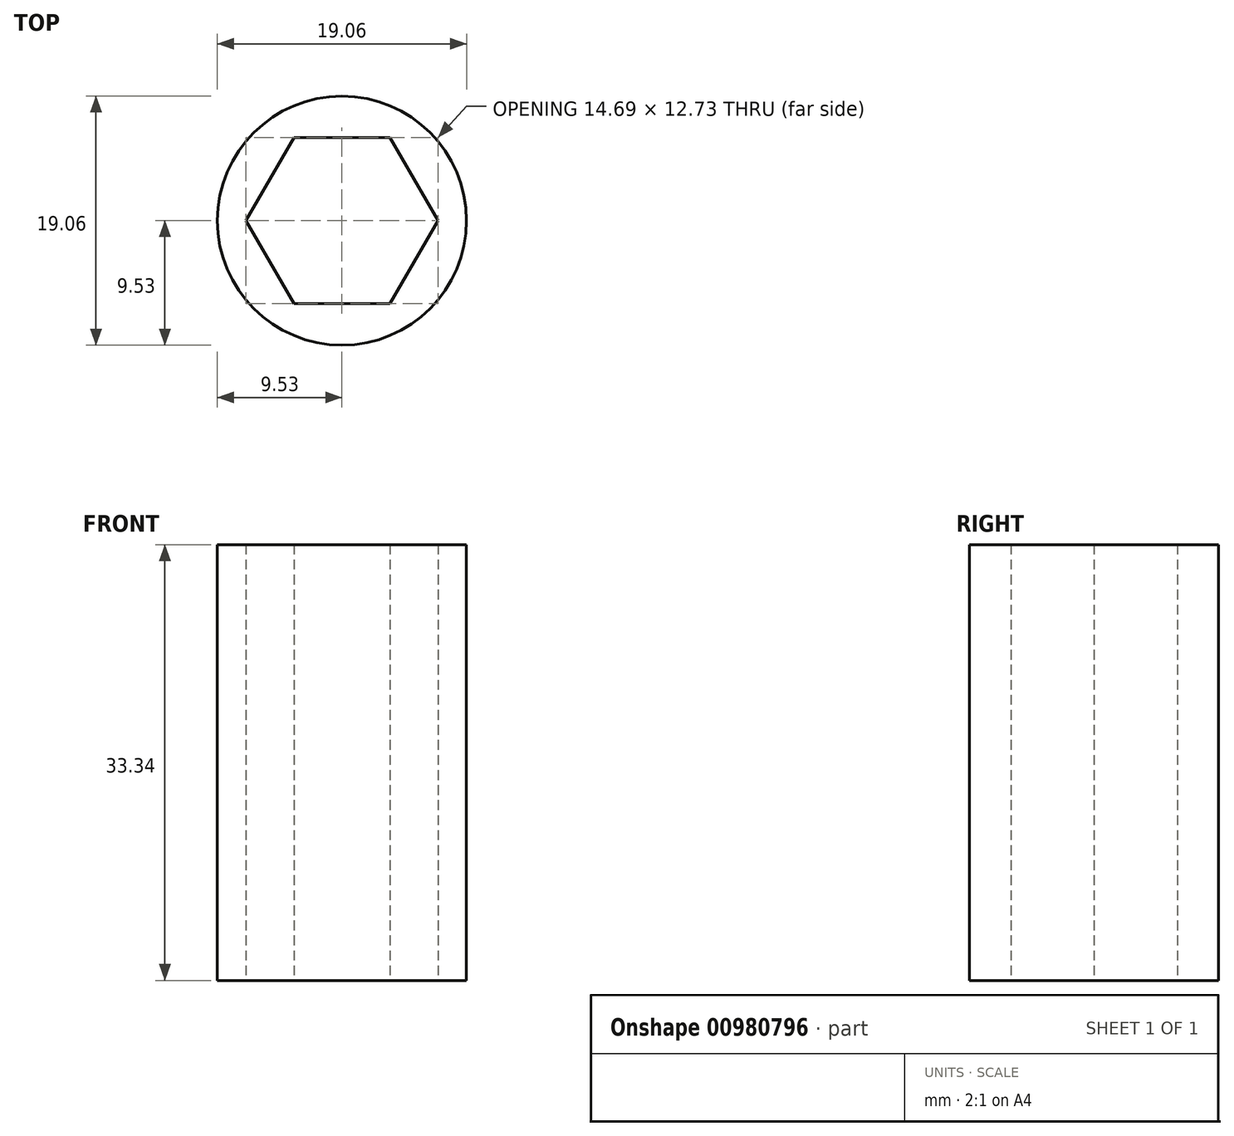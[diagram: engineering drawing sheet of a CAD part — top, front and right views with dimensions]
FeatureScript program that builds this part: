
annotation { "Feature Type Name" : "Feature", "Feature Type Description" : "" }
export const myFeature = defineFeature(function(context is Context, id is Id, definition is map)
    precondition{}
    {
        {
            var Q0;
            Q0=qCreatedBy(makeId("Top.planeOp"),FACE);
            var sketch = newSketch(context, id + "F0", { "sketchPlane" : qUnion([Q0])});
            skCircle(sketch, "E0", {"center": v(0, 0) * mm, "radius": 9.53 * mm});
            skCircle(sketch, "E1.cCircle", {"center": v(0, 0) * mm, "radius": 6.36 * mm, "construction": true});
            skLineSegment(sketch, "E1.0", {"start": v(-3.67, 6.36) * mm, "end": v(3.67, 6.36) * mm});
            skLineSegment(sketch, "E1.1", {"start": v(3.67, 6.36) * mm, "end": v(7.35, 0) * mm});
            skLineSegment(sketch, "E1.2", {"start": v(7.35, 0) * mm, "end": v(3.67, -6.36) * mm});
            skLineSegment(sketch, "E1.3", {"start": v(3.67, -6.36) * mm, "end": v(-3.67, -6.36) * mm});
            skLineSegment(sketch, "E1.4", {"start": v(-3.67, -6.36) * mm, "end": v(-7.35, 0) * mm});
            skLineSegment(sketch, "E1.5", {"start": v(-7.35, 0) * mm, "end": v(-3.67, 6.36) * mm});
            skPoint(sketch, "E1.0.midPoint", {"position": v(0, 6.36) * mm});
            skSolve(sketch);
        }
        {
            var Q0;
            Q0 = qSketchRegion(id + "F0", true);
            extrude(context, id + "F1", {"entities" : qUnion([Q0]), "depth" : 33.34 * mm, "offsetDistance" : 25.4 * mm});
        }
    });
